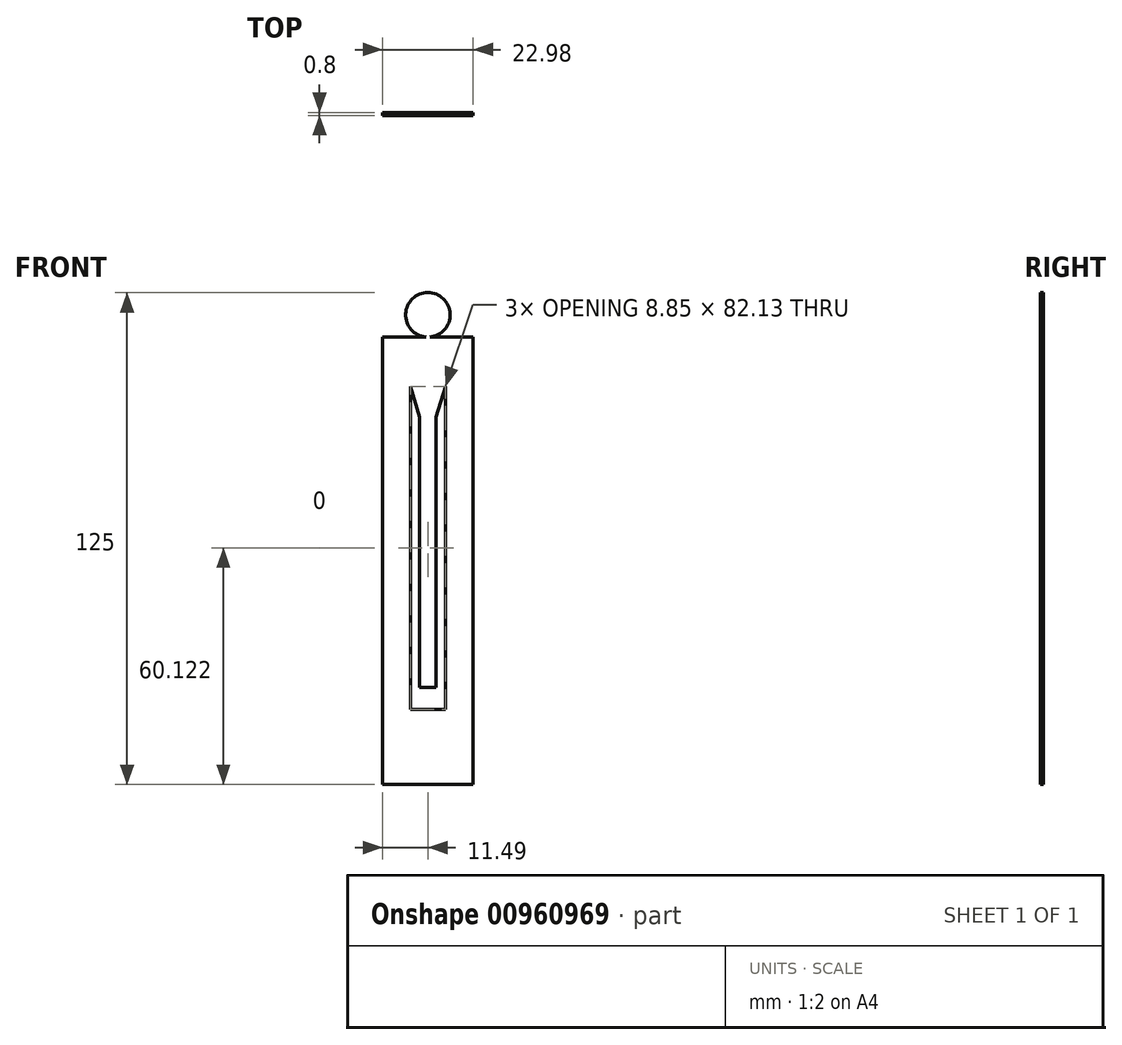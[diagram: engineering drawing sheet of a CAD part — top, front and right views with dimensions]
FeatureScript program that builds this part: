
annotation { "Feature Type Name" : "Feature", "Feature Type Description" : "" }
export const myFeature = defineFeature(function(context is Context, id is Id, definition is map)
    precondition{}
    {
        {
            var Q0;
            Q0=qCreatedBy(makeId("Front.planeOp"),FACE);
            var sketch = newSketch(context, id + "F0", { "sketchPlane" : qUnion([Q0])});
            skCircle(sketch, "E0", {"center": v(0, 25.96) * mm, "radius": 5.65 * mm});
            skLineSegment(sketch, "E1.bottom", {"start": v(-11.49, 20.33) * mm, "end": v(11.49, 20.33) * mm});
            skLineSegment(sketch, "E1.top", {"start": v(-11.49, -93.39) * mm, "end": v(11.49, -93.39) * mm});
            skLineSegment(sketch, "E1.left", {"start": v(-11.49, 20.33) * mm, "end": v(-11.49, -93.39) * mm});
            skLineSegment(sketch, "E1.right", {"start": v(11.49, 20.33) * mm, "end": v(11.49, -93.39) * mm});
            skLineSegment(sketch, "E2", {"start": v(-4.42, 7.8) * mm, "end": v(-4.42, -93.39) * mm});
            skLineSegment(sketch, "E3", {"start": v(-4.42, 7.8) * mm, "end": v(-2.07, 0) * mm});
            skLineSegment(sketch, "E4", {"start": v(-2.07, 0) * mm, "end": v(-2.07, -93.39) * mm});
            skPoint(sketch, "E4.endSnap0", {"position": v(0, -93.39) * mm});
            skLineSegment(sketch, "E5.MirrorCS", {"start": v(2.07, 0) * mm, "end": v(2.07, -93.39) * mm});
            skLineSegment(sketch, "E6.MirrorCS", {"start": v(4.42, 7.8) * mm, "end": v(2.07, 0) * mm});
            skLineSegment(sketch, "E7.MirrorCS", {"start": v(4.42, 7.8) * mm, "end": v(4.42, -93.39) * mm});
            skLineSegment(sketch, "E8", {"start": v(-4.42, -74.33) * mm, "end": v(4.42, -74.33) * mm});
            skLineSegment(sketch, "E9", {"start": v(-2.07, -68.69) * mm, "end": v(2.07, -68.69) * mm});
            skSolve(sketch);
        }
        {
            var Q0;
            {var subQ1=sQuery(id+"F0.wireOp",EDGE,"E1.left");Q0=makeQuery(id+"F0.imprint","IMPRINT",FACE,{"disambiguationData":[TD([[makeQuery(id+"F0.imprint","IMPRINT",EDGE,{"derivedFrom":subQ1}),1.0]])]});}
            var Q1;
            {var subQ0=sQuery(id+"F0.wireOp",EDGE,"E1.bottom");var subQ1=sQuery(id+"F0.wireOp",EDGE,"E0");var subQ2=makeQuery(id+"F0.imprint","INTERSECT",VERTEX,{"disambiguationData":[OD(0.0)],"derivedFrom":[subQ1,subQ0]});Q1=makeQuery(id+"F0.imprint","IMPRINT",FACE,{"disambiguationData":[TD([[makeQuery(id+"F0.imprint","IMPRINT",EDGE,{"disambiguationData":[TD([[subQ2,1.0]])],"derivedFrom":subQ1}),1.0]])]});}
            var Q2;
            {var subQ0=sQuery(id+"F0.wireOp",EDGE,"E1.bottom");var subQ1=sQuery(id+"F0.wireOp",EDGE,"E0");var subQ2=makeQuery(id+"F0.imprint","INTERSECT",VERTEX,{"disambiguationData":[OD(0.0)],"derivedFrom":[subQ1,subQ0]});Q2=makeQuery(id+"F0.imprint","IMPRINT",FACE,{"disambiguationData":[TD([[makeQuery(id+"F0.imprint","IMPRINT",EDGE,{"disambiguationData":[TD([[subQ2,-1.0]])],"derivedFrom":subQ1}),1.0]])]});}
            var Q3;
            {var subQ0=sQuery(id+"F0.wireOp",EDGE,"E5.MirrorCS");var subQ1=sQuery(id+"F0.wireOp",EDGE,"E1.top");var subQ2=makeQuery(id+"F0.imprint","INTERSECT",VERTEX,{"derivedFrom":[subQ1,subQ0]});Q3=makeQuery(id+"F0.imprint","IMPRINT",FACE,{"disambiguationData":[TD([[makeQuery(id+"F0.imprint","IMPRINT",EDGE,{"disambiguationData":[TD([[subQ2,-1.0]])],"derivedFrom":subQ1}),1.0]])]});}
            var Q4;
            {var subQ0=sQuery(id+"F0.wireOp",EDGE,"E4");var subQ1=sQuery(id+"F0.wireOp",EDGE,"E1.top");var subQ2=makeQuery(id+"F0.imprint","INTERSECT",VERTEX,{"derivedFrom":[subQ1,subQ0]});Q4=makeQuery(id+"F0.imprint","IMPRINT",FACE,{"disambiguationData":[TD([[makeQuery(id+"F0.imprint","IMPRINT",EDGE,{"disambiguationData":[TD([[subQ2,-1.0]])],"derivedFrom":subQ1}),1.0]])]});}
            var Q5;
            {var subQ0=sQuery(id+"F0.wireOp",EDGE,"E2");var subQ1=sQuery(id+"F0.wireOp",EDGE,"E1.top");var subQ2=makeQuery(id+"F0.imprint","INTERSECT",VERTEX,{"derivedFrom":[subQ1,subQ0]});Q5=makeQuery(id+"F0.imprint","IMPRINT",FACE,{"disambiguationData":[TD([[makeQuery(id+"F0.imprint","IMPRINT",EDGE,{"disambiguationData":[TD([[subQ2,-1.0]])],"derivedFrom":subQ1}),1.0]])]});}
            extrude(context, id + "F1", {"entities" : qUnion([Q0, Q1, Q2, Q3, Q4, Q5]), "depth" : .8 * mm, "offsetDistance" : 25 * mm});
        }
    });
